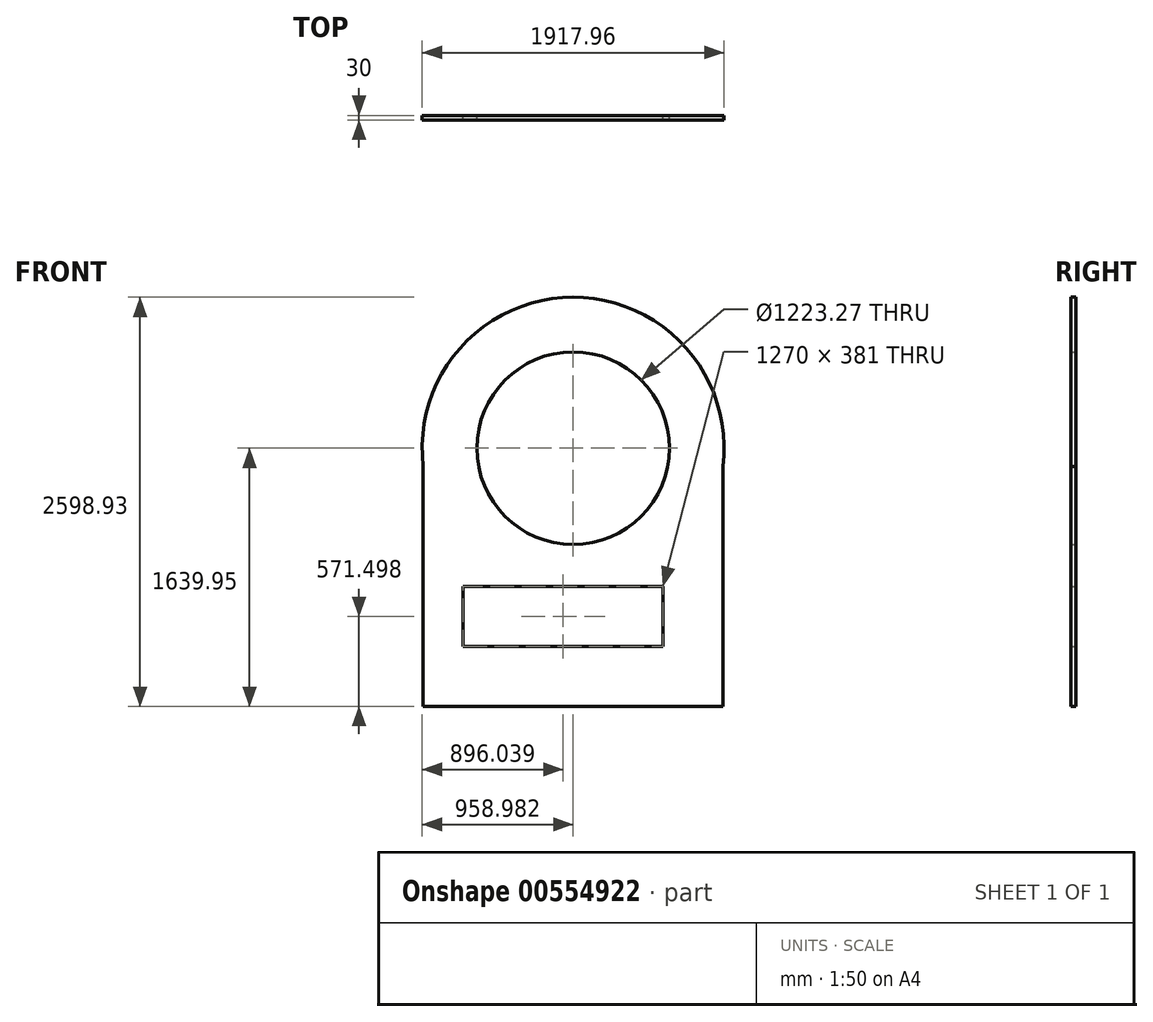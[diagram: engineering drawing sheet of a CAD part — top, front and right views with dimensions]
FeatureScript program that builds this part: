
annotation { "Feature Type Name" : "Feature", "Feature Type Description" : "" }
export const myFeature = defineFeature(function(context is Context, id is Id, definition is map)
    precondition{}
    {
        {
            var Q0;
            Q0=qCreatedBy(makeId("Front.planeOp"),FACE);
            var sketch = newSketch(context, id + "F0", { "sketchPlane" : qUnion([Q0])});
            skLineSegment(sketch, "E0", {"start": v(-991.62, 15.7) * mm, "end": v(-991.62, -1508.3) * mm});
            skLineSegment(sketch, "E1", {"start": v(-991.62, -1508.3) * mm, "end": v(912.26, -1508.3) * mm});
            skLineSegment(sketch, "E2", {"start": v(912.26, -1508.3) * mm, "end": v(912.26, 15.7) * mm});
            skArc(sketch, "E3", {"start": v(912.26, 15.7) * mm, "mid": v(-39.68, 1090.64) * mm, "end": v(-991.62, 15.7) * mm});
            skCircle(sketch, "E4", {"center": v(-39.68, 131.66) * mm, "radius": 611.63 * mm});
            skLineSegment(sketch, "E5.bottom", {"start": v(-737.62, -746.3) * mm, "end": v(532.38, -746.3) * mm});
            skLineSegment(sketch, "E5.top", {"start": v(-737.62, -1127.3) * mm, "end": v(532.38, -1127.3) * mm});
            skLineSegment(sketch, "E5.left", {"start": v(-737.62, -746.3) * mm, "end": v(-737.62, -1127.3) * mm});
            skLineSegment(sketch, "E5.right", {"start": v(532.38, -746.3) * mm, "end": v(532.38, -1127.3) * mm});
            skSolve(sketch);
        }
        {
            var Q0;
            Q0 = qSketchRegion(id + "F0", true);
            extrude(context, id + "F1", {"entities" : qUnion([Q0]), "depth" : 30 * mm, "offsetDistance" : 25.4 * mm});
        }
    });
